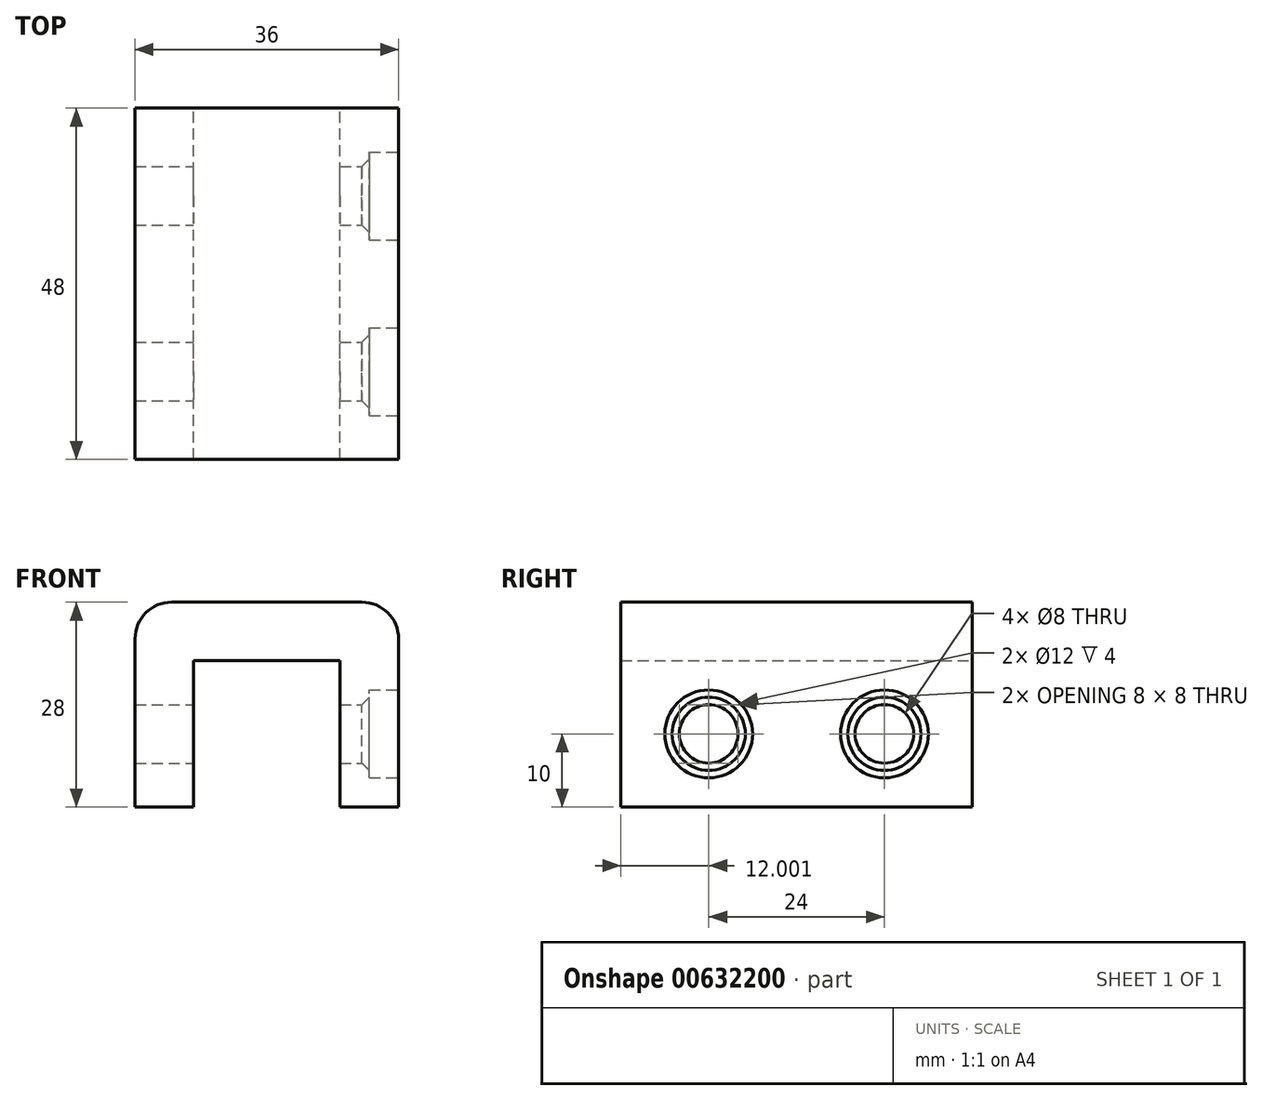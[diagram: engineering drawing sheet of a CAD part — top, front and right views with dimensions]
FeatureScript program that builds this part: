
annotation { "Feature Type Name" : "Feature", "Feature Type Description" : "" }
export const myFeature = defineFeature(function(context is Context, id is Id, definition is map)
    precondition{}
    {
        {
            var Q0;
            Q0=qCreatedBy(makeId("Right.planeOp"),FACE);
            var sketch = newSketch(context, id + "F0", { "sketchPlane" : qUnion([Q0])});
            skLineSegment(sketch, "E0.bottom", {"start": v(-37.15, -28) * mm, "end": v(10.85, -28) * mm});
            skLineSegment(sketch, "E0.top", {"start": v(-37.15, 0) * mm, "end": v(10.85, 0) * mm});
            skLineSegment(sketch, "E0.left", {"start": v(-37.15, -28) * mm, "end": v(-37.15, 0) * mm});
            skLineSegment(sketch, "E0.right", {"start": v(10.85, -28) * mm, "end": v(10.85, 0) * mm});
            skSolve(sketch);
        }
        {
            var Q0;
            Q0=makeQuery(id+"F0.imprint","IMPRINT",FACE,{"disambiguationData":[TD([[makeQuery(id+"F0.imprint","IMPRINT",EDGE,{"derivedFrom":sQuery(id+"F0.wireOp",EDGE,"E0.bottom")}),1.0]])]});
            extrude(context, id + "F1", {"entities" : qUnion([Q0]), "depth" : 36 * mm, "offsetDistance" : 25 * mm});
        }
        {
            var Q0;
            Q0=makeQuery(id+"F1.opExtrude","SWEPT_FACE",FACE,{"disambiguationData":[OSD([sQuery(id+"F0.wireOp",EDGE,"E0.bottom")])]});
            var sketch = newSketch(context, id + "F2", { "sketchPlane" : qUnion([Q0])});
            skLineSegment(sketch, "E1.bottom", {"start": v(8, 37.15) * mm, "end": v(28, 37.15) * mm});
            skLineSegment(sketch, "E1.top", {"start": v(8, -10.85) * mm, "end": v(28, -10.85) * mm});
            skLineSegment(sketch, "E1.left", {"start": v(8, 37.15) * mm, "end": v(8, -10.85) * mm});
            skLineSegment(sketch, "E1.right", {"start": v(28, 37.15) * mm, "end": v(28, -10.85) * mm});
            skSolve(sketch);
        }
        {
            var Q0;
            Q0=makeQuery(id+"F2.imprint","IMPRINT",FACE,{"disambiguationData":[TD([[makeQuery(id+"F2.imprint","IMPRINT",EDGE,{"derivedFrom":sQuery(id+"F2.wireOp",EDGE,"E1.bottom")}),1.0]])]});
            extrude(context, id + "F3", {"entities" : qUnion([Q0]), "operationType" : NewBodyOperationType.REMOVE, "oppositeDirection" : true, "depth" : 20 * mm, "offsetDistance" : 25 * mm});
        }
        {
            var Q0;
            Q0=makeQuery(id+"F1.opExtrude","CAP_EDGE",EDGE,{"disambiguationData":[OSD([sQuery(id+"F0.wireOp",EDGE,"E0.top")])],"isStart":true});
            var Q1;
            Q1=makeQuery(id+"F1.opExtrude","CAP_EDGE",EDGE,{"disambiguationData":[OSD([sQuery(id+"F0.wireOp",EDGE,"E0.top")])],"isStart":false});
            fillet(context, id + "F4", {"entities" : qUnion([Q0, Q1]), "radius" : 5 * mm, "tangentPropagation" : true, "allowEdgeOverflow" : false});
        }
        {
            var Q0;
            Q0=makeQuery(id+"F1.opExtrude","CAP_FACE",FACE,{"disambiguationData":[OSD([sQuery(id+"F0.wireOp",EDGE,"E0.bottom"),sQuery(id+"F0.wireOp",EDGE,"E0.top"),sQuery(id+"F0.wireOp",EDGE,"E0.left"),sQuery(id+"F0.wireOp",EDGE,"E0.right")])],"isStart":false});
            var sketch = newSketch(context, id + "F5", { "sketchPlane" : qUnion([Q0])});
            skCircle(sketch, "E2", {"center": v(46.85, -18) * mm, "radius": 4 * mm});
            skCircle(sketch, "E3.1.0.0", {"center": v(22.85, -18) * mm, "radius": 4 * mm});
            skCircle(sketch, "E3.2.0.0", {"center": v(-1.15, -18) * mm, "radius": 4 * mm});
            skCircle(sketch, "E3.3.0.0", {"center": v(-25.15, -18) * mm, "radius": 4 * mm});
            skLineSegment(sketch, "E3.direction1", {"start": v(46.85, -18) * mm, "end": v(22.85, -18) * mm, "construction": true});
            skSolve(sketch);
        }
        {
            var Q0;
            Q0=qSketchRegion(id+"F5",true);
            extrude(context, id + "F6", {"entities" : qUnion([Q0]), "operationType" : NewBodyOperationType.REMOVE, "oppositeDirection" : true, "depth" : 36 * mm, "offsetDistance" : 25 * mm});
        }
        {
            var Q0;
            Q0=makeQuery(id+"F1.opExtrude","CAP_FACE",FACE,{"disambiguationData":[OSD([sQuery(id+"F0.wireOp",EDGE,"E0.bottom"),sQuery(id+"F0.wireOp",EDGE,"E0.top"),sQuery(id+"F0.wireOp",EDGE,"E0.left"),sQuery(id+"F0.wireOp",EDGE,"E0.right")])],"isStart":false});
            var sketch = newSketch(context, id + "F7", { "sketchPlane" : qUnion([Q0])});
            skCircle(sketch, "E4", {"center": v(-25.15, -18) * mm, "radius": 6 * mm});
            skCircle(sketch, "E5.1.0.0", {"center": v(-1.15, -18) * mm, "radius": 6 * mm});
            skCircle(sketch, "E5.2.0.0", {"center": v(22.85, -18) * mm, "radius": 6 * mm});
            skCircle(sketch, "E5.3.0.0", {"center": v(46.85, -18) * mm, "radius": 6 * mm});
            skLineSegment(sketch, "E5.direction1", {"start": v(-25.15, -18) * mm, "end": v(-1.15, -18) * mm, "construction": true});
            skSolve(sketch);
        }
        {
            var Q0;
            Q0=qSketchRegion(id+"F7",true);
            extrude(context, id + "F8", {"entities" : qUnion([Q0]), "operationType" : NewBodyOperationType.REMOVE, "oppositeDirection" : true, "depth" : 4 * mm, "offsetDistance" : 25 * mm});
        }
        {
            var Q0;
            Q0=makeQuery(id+"F8.boolean.opBoolean","INTERSECT",EDGE,{"derivedFrom":[makeQuery(id+"F6.boolean.opBoolean","COPY",FACE,{"disambiguationData":[TD([makeQuery(id+"F3.boolean.opBoolean","COPY",FACE,{"derivedFrom":makeQuery(id+"F3.opExtrude","SWEPT_FACE",FACE,{"disambiguationData":[OSD([sQuery(id+"F2.wireOp",EDGE,"E1.right")])]})})])],"derivedFrom":makeQuery(id+"F6.opExtrude","SWEPT_FACE",FACE,{"disambiguationData":[OSD([sQuery(id+"F5.wireOp",EDGE,"E3.3.0.0")])]})}),makeQuery(id+"F8.opExtrude","CAP_FACE",FACE,{"disambiguationData":[OSD([sQuery(id+"F7.wireOp",EDGE,"E4")])],"isStart":false})]});
            var Q1;
            Q1=makeQuery(id+"F8.boolean.opBoolean","INTERSECT",EDGE,{"derivedFrom":[makeQuery(id+"F6.boolean.opBoolean","COPY",FACE,{"disambiguationData":[TD([makeQuery(id+"F3.boolean.opBoolean","COPY",FACE,{"derivedFrom":makeQuery(id+"F3.opExtrude","SWEPT_FACE",FACE,{"disambiguationData":[OSD([sQuery(id+"F2.wireOp",EDGE,"E1.right")])]})})])],"derivedFrom":makeQuery(id+"F6.opExtrude","SWEPT_FACE",FACE,{"disambiguationData":[OSD([sQuery(id+"F5.wireOp",EDGE,"E3.2.0.0")])]})}),makeQuery(id+"F8.opExtrude","CAP_FACE",FACE,{"disambiguationData":[OSD([sQuery(id+"F7.wireOp",EDGE,"E5.1.0.0")])],"isStart":false})]});
            var Q2;
            Q2=makeQuery(id+"F8.boolean.opBoolean","INTERSECT",EDGE,{"derivedFrom":[makeQuery(id+"F6.boolean.opBoolean","COPY",FACE,{"disambiguationData":[TD([makeQuery(id+"F3.boolean.opBoolean","COPY",FACE,{"derivedFrom":makeQuery(id+"F3.opExtrude","SWEPT_FACE",FACE,{"disambiguationData":[OSD([sQuery(id+"F2.wireOp",EDGE,"E1.right")])]})})])],"derivedFrom":makeQuery(id+"F6.opExtrude","SWEPT_FACE",FACE,{"disambiguationData":[OSD([sQuery(id+"F5.wireOp",EDGE,"E3.1.0.0")])]})}),makeQuery(id+"F8.opExtrude","CAP_FACE",FACE,{"disambiguationData":[OSD([sQuery(id+"F7.wireOp",EDGE,"E5.2.0.0")])],"isStart":false})]});
            var Q3;
            Q3=makeQuery(id+"F8.boolean.opBoolean","INTERSECT",EDGE,{"derivedFrom":[makeQuery(id+"F6.boolean.opBoolean","COPY",FACE,{"disambiguationData":[TD([makeQuery(id+"F3.boolean.opBoolean","COPY",FACE,{"derivedFrom":makeQuery(id+"F3.opExtrude","SWEPT_FACE",FACE,{"disambiguationData":[OSD([sQuery(id+"F2.wireOp",EDGE,"E1.right")])]})})])],"derivedFrom":makeQuery(id+"F6.opExtrude","SWEPT_FACE",FACE,{"disambiguationData":[OSD([sQuery(id+"F5.wireOp",EDGE,"E2")])]})}),makeQuery(id+"F8.opExtrude","CAP_FACE",FACE,{"disambiguationData":[OSD([sQuery(id+"F7.wireOp",EDGE,"E5.3.0.0")])],"isStart":false})]});
            chamfer(context, id + "F9", {"entities" : qUnion([Q0, Q1, Q2, Q3]), "width" : 1 * mm, "tangentPropagation" : true});
        }
    });
